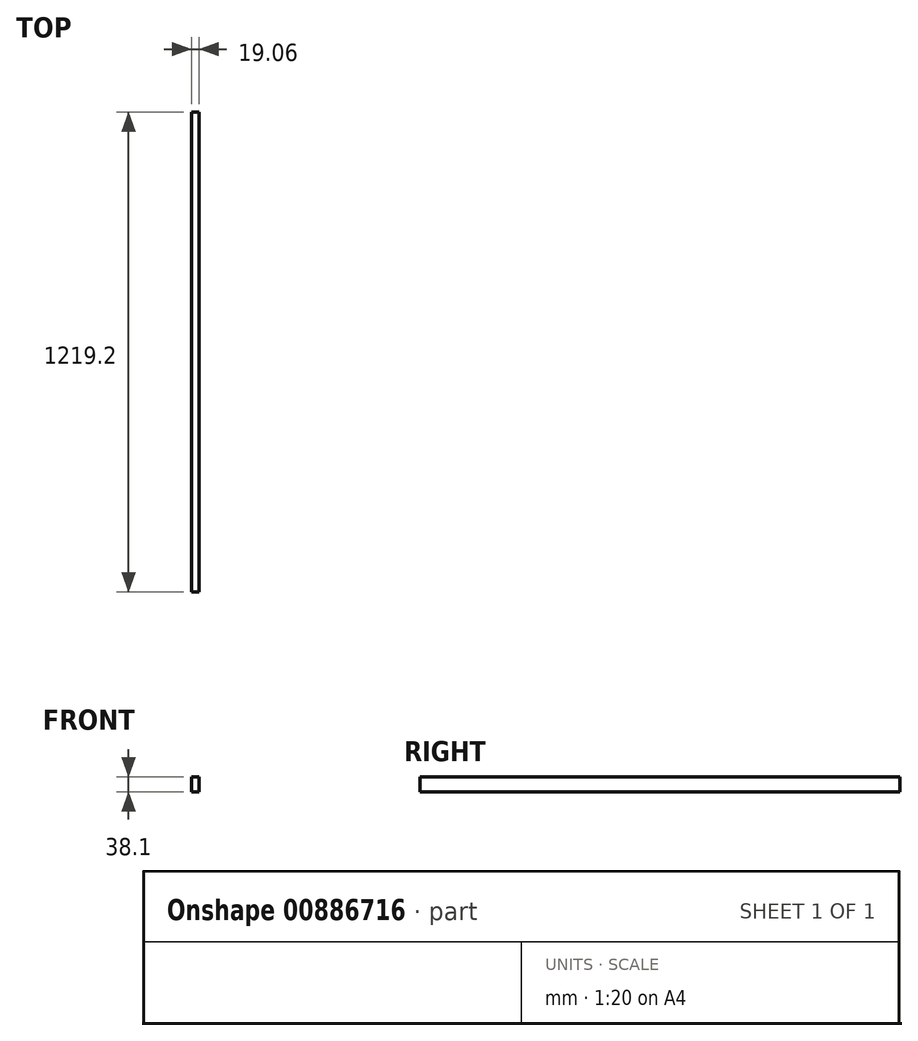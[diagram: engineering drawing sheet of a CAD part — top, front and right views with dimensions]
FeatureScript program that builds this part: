
annotation { "Feature Type Name" : "Feature", "Feature Type Description" : "" }
export const myFeature = defineFeature(function(context is Context, id is Id, definition is map)
    precondition{}
    {
        {
            var Q0;
            Q0=qCreatedBy(makeId("Front.planeOp"),FACE);
            var sketch = newSketch(context, id + "F0", { "sketchPlane" : qUnion([Q0])});
            skLineSegment(sketch, "E0.bottom", {"start": v(9.52, 19.05) * mm, "end": v(-9.53, 19.05) * mm});
            skLineSegment(sketch, "E0.top", {"start": v(9.53, -19.05) * mm, "end": v(-9.52, -19.05) * mm});
            skLineSegment(sketch, "E0.left", {"start": v(9.52, 19.05) * mm, "end": v(9.53, -19.05) * mm});
            skLineSegment(sketch, "E0.right", {"start": v(-9.53, 19.05) * mm, "end": v(-9.52, -19.05) * mm});
            skPoint(sketch, "E0.middle", {"position": v(0, 0) * mm});
            skSolve(sketch);
        }
        {
            var Q0;
            Q0=makeQuery(id+"F0.imprint","IMPRINT",FACE,{"disambiguationData":[TD([[makeQuery(id+"F0.imprint","IMPRINT",EDGE,{"derivedFrom":sQuery(id+"F0.wireOp",EDGE,"E0.bottom")}),1.0]])]});
            extrude(context, id + "F1", {"entities" : qUnion([Q0]), "endBound" : BoundingType.SYMMETRIC, "depth" : 1219.2 * mm, "offsetDistance" : 25.4 * mm});
        }
    });
